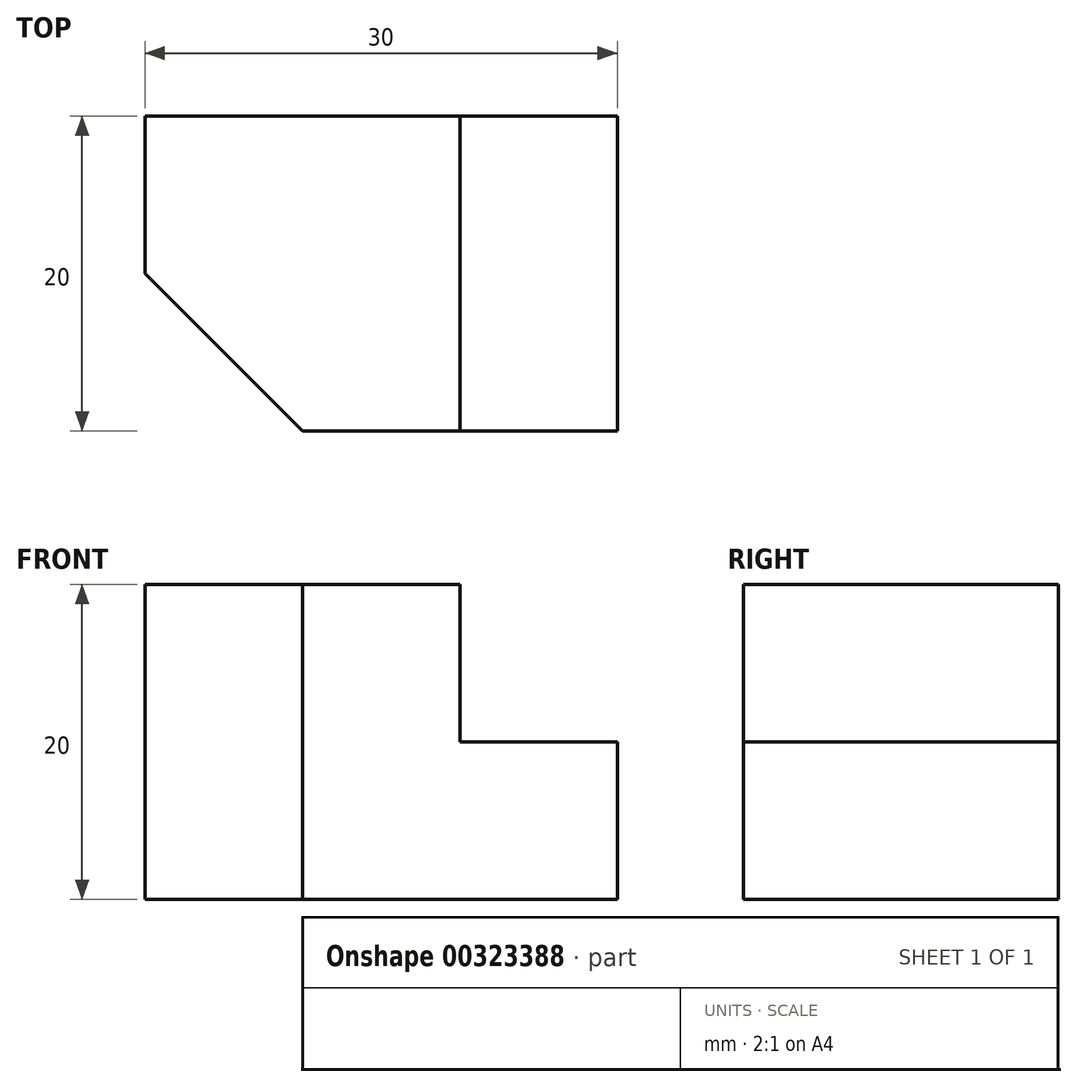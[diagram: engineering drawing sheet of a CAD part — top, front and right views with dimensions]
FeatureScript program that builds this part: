
annotation { "Feature Type Name" : "Feature", "Feature Type Description" : "" }
export const myFeature = defineFeature(function(context is Context, id is Id, definition is map)
    precondition{}
    {
        {
            var Q0;
            Q0=qCreatedBy(makeId("Top.planeOp"),FACE);
            var sketch = newSketch(context, id + "F0", { "sketchPlane" : qUnion([Q0])});
            skLineSegment(sketch, "E0", {"start": v(0, 0) * mm, "end": v(20, 0) * mm});
            skLineSegment(sketch, "E1", {"start": v(20, 0) * mm, "end": v(20, -20) * mm});
            skLineSegment(sketch, "E2", {"start": v(20, -20) * mm, "end": v(10, -20) * mm});
            skLineSegment(sketch, "E3", {"start": v(10, -20) * mm, "end": v(0, -10) * mm});
            skLineSegment(sketch, "E4", {"start": v(0, -10) * mm, "end": v(0, 0) * mm});
            skSolve(sketch);
        }
        {
            var Q0;
            Q0 = qSketchRegion(id + "F0", true);
            extrude(context, id + "F1", {"entities" : qUnion([Q0]), "depth" : 20 * mm});
        }
        {
            var Q0;
            Q0=makeQuery(id+"F1.opExtrude","SWEPT_FACE",FACE,{"disambiguationData":[OSD([sQuery(id+"F0.wireOp",EDGE,"E2")])]});
            var sketch = newSketch(context, id + "F2", { "sketchPlane" : qUnion([Q0])});
            skLineSegment(sketch, "E5", {"start": v(20, 0) * mm, "end": v(30, 0) * mm});
            skLineSegment(sketch, "E6", {"start": v(30, 0) * mm, "end": v(30, 10) * mm});
            skLineSegment(sketch, "E7", {"start": v(30, 10) * mm, "end": v(20, 10) * mm});
            skLineSegment(sketch, "E8", {"start": v(20, 10) * mm, "end": v(20, 0) * mm});
            skSolve(sketch);
        }
        {
            var Q0;
            Q0 = qSketchRegion(id + "F2", true);
            extrude(context, id + "F3", {"entities" : qUnion([Q0]), "operationType" : NewBodyOperationType.ADD, "oppositeDirection" : true, "depth" : 20 * mm});
        }
    });
